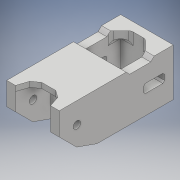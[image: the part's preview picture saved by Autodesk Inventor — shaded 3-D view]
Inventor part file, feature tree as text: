
AUTODESK INVENTOR PART (.ipt)
format: ipt  version: 2018 (Build 220112000, 112)  size: 322,048 bytes
history: native  units: mm
features: extrude x13, sketch x13, chamfer x4, projected_geometry x4, fillet x1
ambient origin geometry x8: Origin, YZ Plane, XZ Plane, XY Plane, X Axis, Y Axis, Z Axis, Center Point
bodies: Solid1 (feature_tree)
feature tree (35):
  extrude  "Extrusion1"  Depth=21.9mm
  extrude  "Extrusion2"  Depth=5.0mm
  extrude  "Extrusion3"  Depth=18.1mm
  extrude  "Extrusion4"  Depth=27.0mm TaperAngle=0.0deg
  extrude  "Extrusion5"  Depth=7.0mm
  extrude  "Extrusion6"  Depth=20.0mm
  chamfer  "Chamfer1"  Distance=14.0mm
  extrude  "Extrusion7"  Depth=5.0mm
  extrude  "Extrusion8"  Depth=4.0mm TaperAngle=0.0deg
  chamfer  "Chamfer2"  Distance=4.0mm
  extrude  "Extrusion9"  Depth=4.0mm
  chamfer  "Chamfer3"  Distance=4.2mm
  extrude  "Extrusion10"  Depth=10.0mm
  extrude  "Extrusion11"  Depth=15.0mm
  extrude  "Extrusion12"  Depth=4.0mm TaperAngle=0.0deg
  chamfer  "Chamfer4"  Distance=9.0mm
  extrude  "Extrusion13"  Depth=3.0mm
  fillet  "Fillet1"  Radius=4.0mm
  sketch  "Sketch1"  dims[d0=20.0mm d1=21.9mm]
  sketch  "Sketch3"  dims[d2=5.0mm d3=5.0mm]
  sketch  "Sketch4"  dims[d4=5.0mm d5=18.1mm]
  sketch  "Sketch5"  dims[d6=20.0mm d7=27.0mm d8=0.0mm]
  sketch  "Sketch6"  dims[d9=5.2mm d10=7.0mm]
  sketch  "Sketch7"  dims[d11=20.0mm d12=0.0mm d13=9.3mm]
  projected_geometry  "Projected Loop1"
  sketch  "Sketch8"  dims[d14=8.3mm]
  sketch  "Sketch9"  dims[d15=8.3mm d16=14.0mm d17=0.0mm]
  projected_geometry  "Projected Loop2"
  sketch  "Sketch10"  dims[d18=3.0mm d19=0.0mm d20=5.0mm]
  projected_geometry  "Projected Loop3"
  sketch  "Sketch11"  dims[d21=12.0mm d23=4.0mm d24=0.0mm]
  sketch  "Sketch12"  dims[d25=5.0mm]
  sketch  "Sketch13"  dims[d26=12.0mm d27=4.0mm d28=0.0mm]
  projected_geometry  "Projected Loop4"
  sketch  "Sketch14"  dims[d29=1.0mm d30=2.0mm d31=45.0deg d32=4.0mm d33=4.2mm d34=10.0mm d35=15.0mm d36=4.0mm d37=0.0mm d38=9.0mm d39=3.0mm d40=4.0mm d41=0.0mm d42=3.0mm d43=2.0mm d44=45.0deg d45=6.5mm d46=12.0mm d47=10.0mm d48=0.0mm d49=4.0mm d50=2.0mm d51=45.0deg d52=13.0mm d53=9.0mm d54=12.0mm d55=0.0mm d56=45.0deg d57=14.0mm d58=4.1mm d59=7.5mm d60=12.0mm d61=0.0mm d62=2.0mm d63=2.0mm d64=12.0mm d65=0.0mm d66=2.0mm d67=2.0mm d68=45.0deg d69=45.0deg d70=4.0mm d71=0.0mm d72=2.8mm]
